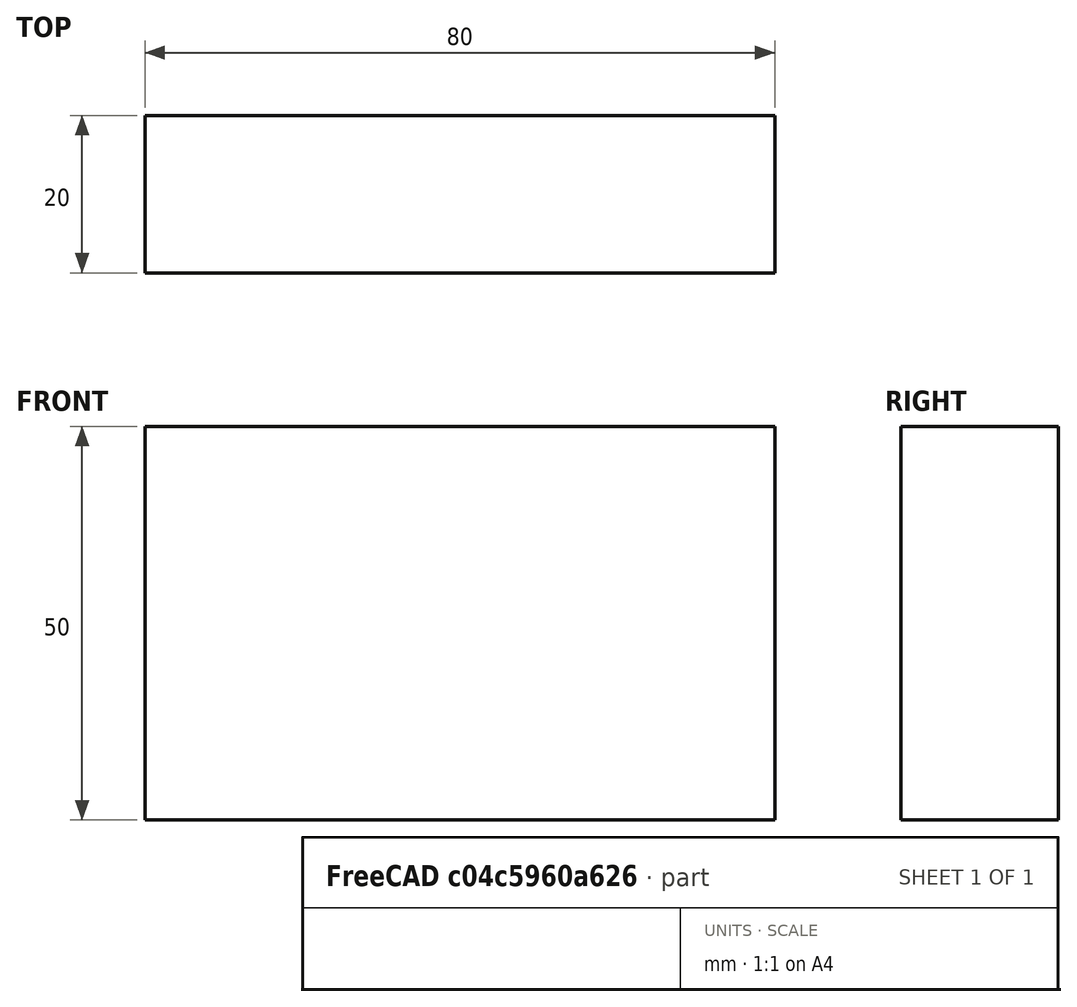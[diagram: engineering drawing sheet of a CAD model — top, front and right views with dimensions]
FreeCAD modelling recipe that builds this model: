
FCSTD DOCUMENT  (FreeCAD 0.15R4671 (Git))
Label: Flat Bar 80x20 EN10058 S235JR
License: All rights reserved
LicenseURL: http://en.wikipedia.org/wiki/All_rights_reserved
objects: Sketcher::SketchObject×1, Part::Extrusion×1
note: 2 computed .brp shape members not serialized (recipe doc carries the construction recipe); baked Part::Feature solids carry a one-line shape summary decoded from their .brp

FEATURE [Sketcher::SketchObject] Sketch
  sketch-geometry (4):
    g0: LineSegment StartX=-40 StartY=-10 StartZ=0 EndX=40 EndY=-10 EndZ=0
    g1: LineSegment StartX=40 StartY=-10 StartZ=0 EndX=40 EndY=10 EndZ=0
    g2: LineSegment StartX=40 StartY=10 StartZ=0 EndX=-40 EndY=10 EndZ=0
    g3: LineSegment StartX=-40 StartY=10 StartZ=0 EndX=-40 EndY=-10 EndZ=0
  constraints (12):
    c: Coincident(g0,g1)
    c: Coincident(g1,g2)
    c: Coincident(g2,g3)
    c: Coincident(g3,g0)
    c: Horizontal(g0)
    c: Horizontal(g2)
    c: Vertical(g1)
    c: Vertical(g3)
    c: Symmetric(g1,g2,g-2)
    c: Symmetric(g0,g1,g-1)
    c: DistanceY(g1) = 20
    c: DistanceX(g0) = 80
FEATURE [Part::Extrusion] Extrude  label="Flat Bar 80x20 EN10058 S235JR"
  Base = -> Sketch
  Dir = (0,0,50)
  Solid = true
